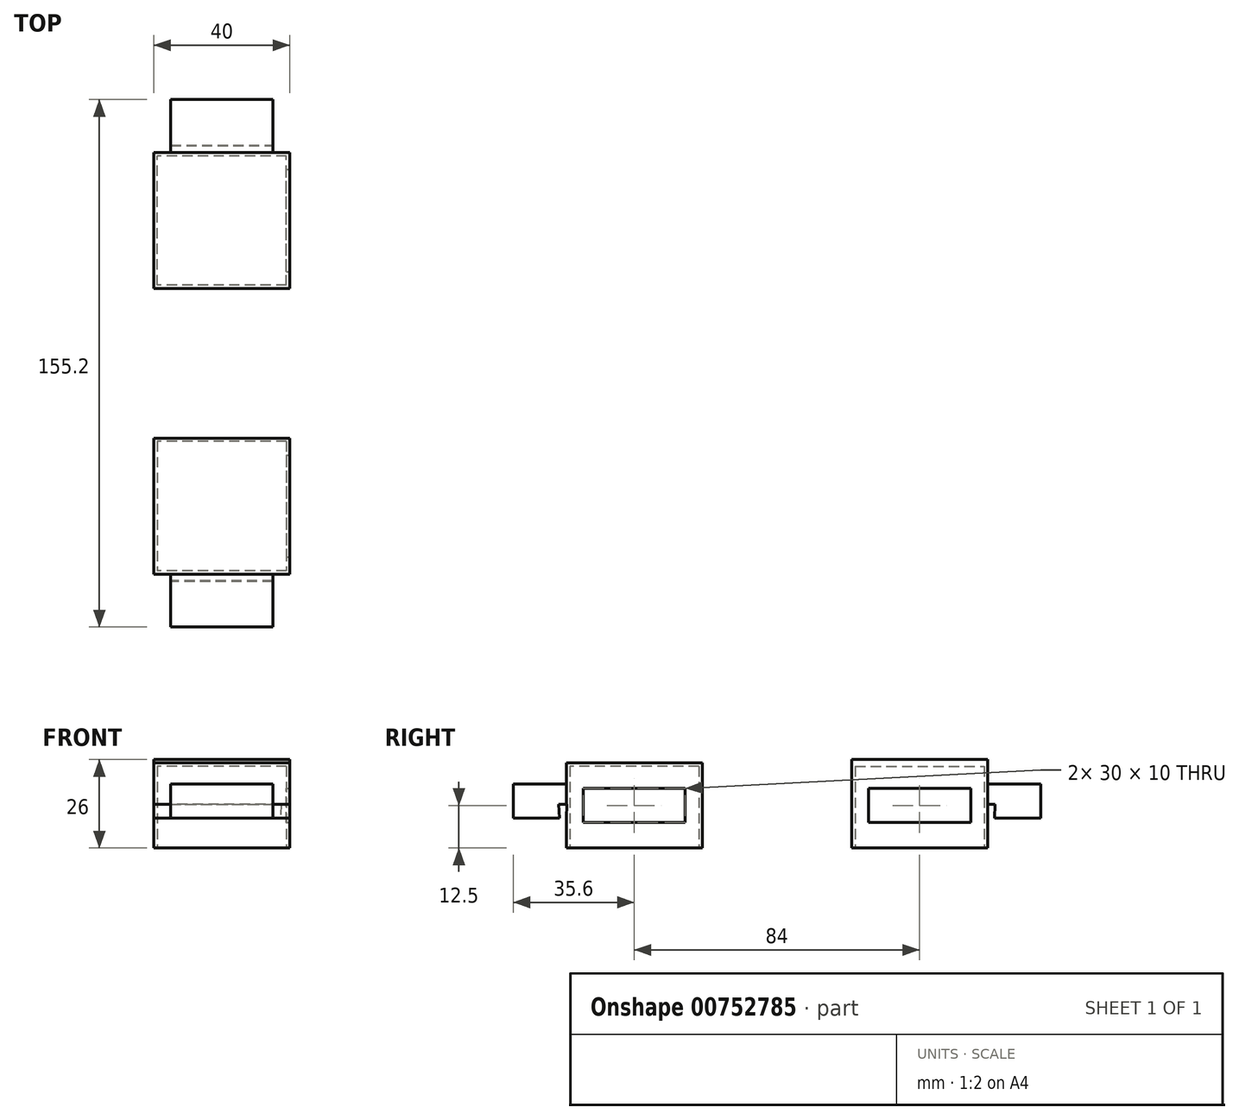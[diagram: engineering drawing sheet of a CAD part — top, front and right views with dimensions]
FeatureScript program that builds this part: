
annotation { "Feature Type Name" : "Feature", "Feature Type Description" : "" }
export const myFeature = defineFeature(function(context is Context, id is Id, definition is map)
    precondition{}
    {
        {
            var Q0;
            Q0=qCreatedBy(makeId("Top.planeOp"),FACE);
            var sketch = newSketch(context, id + "F0", { "sketchPlane" : qUnion([Q0])});
            skLineSegment(sketch, "E0.bottom", {"start": v(20, 20) * mm, "end": v(-20, 20) * mm});
            skLineSegment(sketch, "E0.top", {"start": v(20, -20) * mm, "end": v(-20, -20) * mm});
            skLineSegment(sketch, "E0.left", {"start": v(20, 20) * mm, "end": v(20, -20) * mm});
            skLineSegment(sketch, "E0.right", {"start": v(-20, 20) * mm, "end": v(-20, -20) * mm});
            skPoint(sketch, "E0.middle", {"position": v(0, 0) * mm});
            skSolve(sketch);
        }
        {
            var Q0;
            Q0=makeQuery(id+"F0.imprint","IMPRINT",FACE,{"disambiguationData":[TD([[makeQuery(id+"F0.imprint","IMPRINT",EDGE,{"derivedFrom":sQuery(id+"F0.wireOp",EDGE,"E0.bottom")}),1.0]])]});
            extrude(context, id + "F1", {"entities" : qUnion([Q0]), "depth" : 25 * mm, "offsetDistance" : 25 * mm});
        }
        {
            var Q0;
            Q0=makeQuery(id+"F1.opExtrude","CAP_FACE",FACE,{"disambiguationData":[OSD([sQuery(id+"F0.wireOp",EDGE,"E0.bottom"),sQuery(id+"F0.wireOp",EDGE,"E0.top"),sQuery(id+"F0.wireOp",EDGE,"E0.left"),sQuery(id+"F0.wireOp",EDGE,"E0.right")])],"isStart":true});
            shell(context, id + "F2", {"entities" : qUnion([Q0]), "thickness" : 1 * mm});
        }
        {
            var Q0;
            Q0=makeQuery(id+"F1.opExtrude","SWEPT_FACE",FACE,{"disambiguationData":[OSD([sQuery(id+"F0.wireOp",EDGE,"E0.top")])]});
            var sketch = newSketch(context, id + "F3", { "sketchPlane" : qUnion([Q0])});
            skLineSegment(sketch, "E1.bottom", {"start": v(15, 18.8) * mm, "end": v(-15, 18.8) * mm});
            skLineSegment(sketch, "E1.top", {"start": v(15, 8.8) * mm, "end": v(-15, 8.8) * mm});
            skLineSegment(sketch, "E1.left", {"start": v(15, 18.8) * mm, "end": v(15, 8.8) * mm});
            skLineSegment(sketch, "E1.right", {"start": v(-15, 18.8) * mm, "end": v(-15, 8.8) * mm});
            skPoint(sketch, "E1.middle", {"position": v(0, 13.8) * mm});
            skSolve(sketch);
        }
        {
            var Q0;
            Q0=makeQuery(id+"F1.opExtrude","SWEPT_FACE",FACE,{"disambiguationData":[OSD([sQuery(id+"F0.wireOp",EDGE,"E0.left")])]});
            var sketch = newSketch(context, id + "F4", { "sketchPlane" : qUnion([Q0])});
            skLineSegment(sketch, "E2.bottom", {"start": v(15, 7.5) * mm, "end": v(-15, 7.5) * mm});
            skLineSegment(sketch, "E2.top", {"start": v(15, 17.5) * mm, "end": v(-15, 17.5) * mm});
            skLineSegment(sketch, "E2.left", {"start": v(15, 7.5) * mm, "end": v(15, 17.5) * mm});
            skLineSegment(sketch, "E2.right", {"start": v(-15, 7.5) * mm, "end": v(-15, 17.5) * mm});
            skPoint(sketch, "E2.middle", {"position": v(0, 12.5) * mm});
            skPoint(sketch, "E2.middle.positionSnap0", {"position": v(-20, 12.5) * mm});
            skPoint(sketch, "E2.centerSnap0", {"position": v(-20, 12.5) * mm});
            skSolve(sketch);
        }
        {
            var Q0;
            Q0=makeQuery(id+"F3.imprint","IMPRINT",FACE,{"disambiguationData":[TD([[makeQuery(id+"F3.imprint","IMPRINT",EDGE,{"derivedFrom":sQuery(id+"F3.wireOp",EDGE,"E1.bottom")}),1.0]])]});
            extrude(context, id + "F5", {"entities" : qUnion([Q0]), "operationType" : NewBodyOperationType.ADD, "depth" : 15.6 * mm, "offsetDistance" : 25 * mm});
        }
        {
            var Q0;
            Q0=makeQuery(id+"F4.imprint","IMPRINT",FACE,{"disambiguationData":[TD([[makeQuery(id+"F4.imprint","IMPRINT",EDGE,{"derivedFrom":sQuery(id+"F4.wireOp",EDGE,"E2.bottom")}),-1.0]])]});
            extrude(context, id + "F6", {"entities" : qUnion([Q0]), "operationType" : NewBodyOperationType.REMOVE, "oppositeDirection" : true, "depth" : 25 * mm, "offsetDistance" : 25 * mm});
        }
        {
            var Q0;
            Q0=qCreatedBy(makeId("Front.planeOp"),FACE);
            cPlane(context, id + "F7", {"entities" : qUnion([Q0]), "cplaneType" : CPlaneType.OFFSET, "offset" : 42 * mm, "oppositeDirection" : true, "width" : 150 * mm, "height" : 150 * mm});
        }
        {
            var Q0;
            Q0=makeQuery(id+"F1.opExtrude","SWEPT_BODY",BODY,{"disambiguationData":[OSD([sQuery(id+"F0.wireOp",EDGE,"E0.bottom"),sQuery(id+"F0.wireOp",EDGE,"E0.top"),sQuery(id+"F0.wireOp",EDGE,"E0.left"),sQuery(id+"F0.wireOp",EDGE,"E0.right")])]});
            var Q1;
            Q1=qCreatedBy(id+"F7.planeOp",FACE);
            mirror(context, id + "F8", {"entities" : qUnion([Q0]), "mirrorPlane" : qUnion([Q1])});
        }
        {
            var Q0;
            Q0=makeQuery(id+"F8.opPattern","COPY",FACE,{"derivedFrom":makeQuery(id+"F1.opExtrude","CAP_FACE",FACE,{"disambiguationData":[OSD([sQuery(id+"F0.wireOp",EDGE,"E0.bottom"),sQuery(id+"F0.wireOp",EDGE,"E0.top"),sQuery(id+"F0.wireOp",EDGE,"E0.left"),sQuery(id+"F0.wireOp",EDGE,"E0.right")])],"isStart":false}),"instanceName":"1"});
            extrude(context, id + "F9", {"entities" : qUnion([Q0]), "operationType" : NewBodyOperationType.ADD, "depth" : 1 * mm, "offsetDistance" : 25 * mm});
        }
        {
            var Q0;
            Q0=makeQuery(id+"F5.opExtrude","SWEPT_FACE",FACE,{"disambiguationData":[OSD([sQuery(id+"F3.wireOp",EDGE,"E1.top")])]});
            var sketch = newSketch(context, id + "F10", { "sketchPlane" : qUnion([Q0])});
            skLineSegment(sketch, "E3.left", {"start": v(15, 20) * mm, "end": v(15, 20) * mm});
            skLineSegment(sketch, "E3.right", {"start": v(-15, 20) * mm, "end": v(-15, 20) * mm});
            skPoint(sketch, "E3.middle", {"position": v(0, 20) * mm});
            skLineSegment(sketch, "E4.bottom", {"start": v(23.85, 20) * mm, "end": v(-23.85, 20) * mm});
            skLineSegment(sketch, "E4.top", {"start": v(23.85, 22) * mm, "end": v(-23.85, 22) * mm});
            skLineSegment(sketch, "E4.left", {"start": v(23.85, 20) * mm, "end": v(23.85, 22) * mm});
            skLineSegment(sketch, "E4.right", {"start": v(-23.85, 20) * mm, "end": v(-23.85, 22) * mm});
            skPoint(sketch, "E4.middle", {"position": v(0, 21) * mm});
            skSolve(sketch);
        }
        {
            var Q0;
            Q0 = qSketchRegion(id + "F10", true);
            extrude(context, id + "F11", {"entities" : qUnion([Q0]), "operationType" : NewBodyOperationType.REMOVE, "oppositeDirection" : true, "depth" : 4 * mm, "offsetDistance" : 25 * mm, "hasDraft" : true, "draftAngle" : 3 * degree});
        }
        {
            var Q0;
            Q0=makeQuery(id+"F8.opPattern","COPY",FACE,{"derivedFrom":makeQuery(id+"F5.opExtrude","SWEPT_FACE",FACE,{"disambiguationData":[OSD([sQuery(id+"F3.wireOp",EDGE,"E1.top")])]}),"instanceName":"1"});
            var sketch = newSketch(context, id + "F12", { "sketchPlane" : qUnion([Q0])});
            skLineSegment(sketch, "E5.left", {"start": v(8.4, -112.14) * mm, "end": v(8.4, -112.14) * mm});
            skLineSegment(sketch, "E5.right", {"start": v(-21.6, -112.14) * mm, "end": v(-21.6, -112.14) * mm});
            skPoint(sketch, "E5.middle", {"position": v(-6.6, -112.14) * mm});
            skLineSegment(sketch, "E6.bottom", {"start": v(17.25, -106) * mm, "end": v(-30.44, -106) * mm});
            skLineSegment(sketch, "E6.top", {"start": v(17.25, -104) * mm, "end": v(-30.44, -104) * mm});
            skLineSegment(sketch, "E6.left", {"start": v(17.25, -106) * mm, "end": v(17.25, -104) * mm});
            skLineSegment(sketch, "E6.right", {"start": v(-30.44, -106) * mm, "end": v(-30.44, -104) * mm});
            skPoint(sketch, "E6.middle", {"position": v(-6.6, -105) * mm});
            skSolve(sketch);
        }
        {
            var Q0;
            Q0 = qSketchRegion(id + "F12", true);
            extrude(context, id + "F13", {"entities" : qUnion([Q0]), "operationType" : NewBodyOperationType.REMOVE, "oppositeDirection" : true, "depth" : 4 * mm, "offsetDistance" : 25 * mm, "hasDraft" : true, "draftAngle" : 3 * degree});
        }
    });
